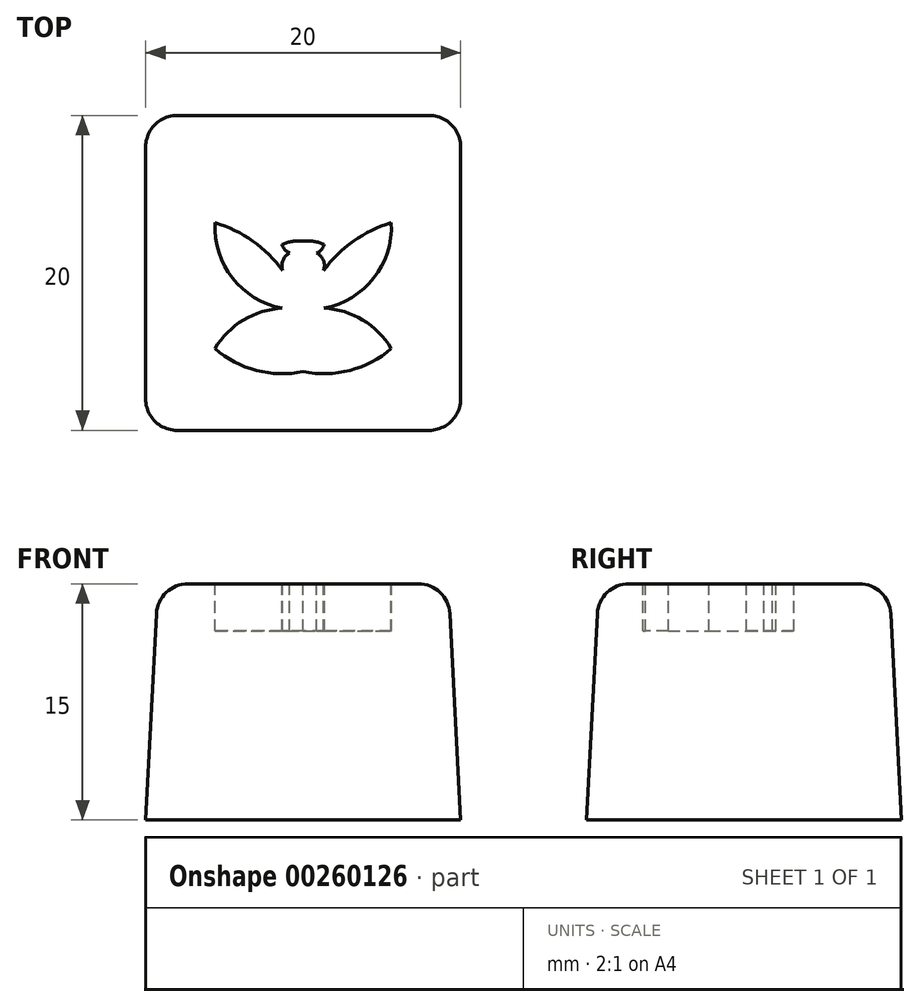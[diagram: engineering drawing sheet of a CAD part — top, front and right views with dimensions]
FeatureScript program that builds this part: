
annotation { "Feature Type Name" : "Feature", "Feature Type Description" : "" }
export const myFeature = defineFeature(function(context is Context, id is Id, definition is map)
    precondition{}
    {
        {
            var Q0;
            Q0=qCreatedBy(makeId("Top.planeOp"),FACE);
            var sketch = newSketch(context, id + "F0", { "sketchPlane" : qUnion([Q0])});
            skLineSegment(sketch, "E0.bottom", {"start": v(-8.66, 8.2) * mm, "end": v(11.34, 8.2) * mm});
            skLineSegment(sketch, "E0.top", {"start": v(-8.66, -11.8) * mm, "end": v(11.34, -11.8) * mm});
            skLineSegment(sketch, "E0.left", {"start": v(-8.66, 8.2) * mm, "end": v(-8.66, -11.8) * mm});
            skLineSegment(sketch, "E0.right", {"start": v(11.34, 8.2) * mm, "end": v(11.34, -11.8) * mm});
            skSolve(sketch);
        }
        {
            var Q0;
            Q0 = qSketchRegion(id + "F0", true);
            extrude(context, id + "F1", {"entities" : qUnion([Q0]), "depth" : 15 * mm, "hasDraft" : true, "draftAngle" : 3 * degree, "draftPullDirection" : true});
        }
        {
            var Q0;
            Q0=makeQuery(id+"F1.opExtrude","CAP_EDGE",EDGE,{"disambiguationData":[OSD([sQuery(id+"F0.wireOp",EDGE,"E0.bottom")])],"isStart":false});
            var Q1;
            Q1=makeQuery(id+"F1.opExtrude","SWEPT_EDGE",EDGE,{"disambiguationData":[OSD([sQuery(id+"F0.wireOp",EDGE,"E0.bottom"),sQuery(id+"F0.wireOp",EDGE,"E0.right")])]});
            var Q2;
            Q2=makeQuery(id+"F1.opExtrude","SWEPT_EDGE",EDGE,{"disambiguationData":[OSD([sQuery(id+"F0.wireOp",EDGE,"E0.top"),sQuery(id+"F0.wireOp",EDGE,"E0.right")])]});
            var Q3;
            Q3=makeQuery(id+"F1.opExtrude","CAP_EDGE",EDGE,{"disambiguationData":[OSD([sQuery(id+"F0.wireOp",EDGE,"E0.right")])],"isStart":false});
            var Q4;
            Q4=makeQuery(id+"F1.opExtrude","CAP_EDGE",EDGE,{"disambiguationData":[OSD([sQuery(id+"F0.wireOp",EDGE,"E0.left")])],"isStart":false});
            var Q5;
            Q5=makeQuery(id+"F1.opExtrude","CAP_EDGE",EDGE,{"disambiguationData":[OSD([sQuery(id+"F0.wireOp",EDGE,"E0.top")])],"isStart":false});
            var Q6;
            Q6=makeQuery(id+"F1.opExtrude","SWEPT_EDGE",EDGE,{"disambiguationData":[OSD([sQuery(id+"F0.wireOp",EDGE,"E0.bottom"),sQuery(id+"F0.wireOp",EDGE,"E0.left")])]});
            var Q7;
            Q7=makeQuery(id+"F1.opExtrude","SWEPT_EDGE",EDGE,{"disambiguationData":[OSD([sQuery(id+"F0.wireOp",EDGE,"E0.top"),sQuery(id+"F0.wireOp",EDGE,"E0.left")])]});
            fillet(context, id + "F2", {"entities" : qUnion([Q0, Q1, Q2, Q3, Q4, Q5, Q6, Q7]), "radius" : 2 * mm, "tangentPropagation" : true, "allowEdgeOverflow" : false});
        }
        {
            var Q0;
            Q0=makeQuery(id+"F1.opExtrude","CAP_FACE",FACE,{"disambiguationData":[OSD([sQuery(id+"F0.wireOp",EDGE,"E0.bottom"),sQuery(id+"F0.wireOp",EDGE,"E0.top"),sQuery(id+"F0.wireOp",EDGE,"E0.left"),sQuery(id+"F0.wireOp",EDGE,"E0.right")])],"isStart":false});
            var sketch = newSketch(context, id + "F3", { "sketchPlane" : qUnion([Q0])});
            skLineSegment(sketch, "E1", {"start": v(1.34, 5.5) * mm, "end": v(1.34, -9.12) * mm});
            skArc(sketch, "E2", {"start": v(-4.26, -6.62) * mm, "mid": v(-1.63, -8) * mm, "end": v(1.34, -8.08) * mm});
            skArc(sketch, "E3", {"start": v(0, -4.05) * mm, "mid": v(-2.45, -4.8) * mm, "end": v(-4.26, -6.62) * mm});
            skArc(sketch, "E4", {"start": v(-4.26, 1.38) * mm, "mid": v(-3.15, -2.14) * mm, "end": v(0, -4.05) * mm});
            skArc(sketch, "E5", {"start": v(0.03, -1.66) * mm, "mid": v(-1.86, 0.21) * mm, "end": v(-4.26, 1.38) * mm});
            skArc(sketch, "E6", {"start": v(0.47, -0.54) * mm, "mid": v(0.05, -1.02) * mm, "end": v(0.03, -1.66) * mm});
            skArc(sketch, "E7", {"start": v(0, 0) * mm, "mid": v(0.17, -0.33) * mm, "end": v(0.47, -0.54) * mm});
            skArc(sketch, "E8", {"start": v(1.34, 0.2) * mm, "mid": v(0.66, 0.19) * mm, "end": v(0, 0) * mm});
            skArc(sketch, "E9.MirrorCS", {"start": v(1.34, 0.2) * mm, "mid": v(2.02, 0.19) * mm, "end": v(2.68, 0) * mm});
            skArc(sketch, "E10.MirrorCS", {"start": v(2.68, 0) * mm, "mid": v(2.5, -0.33) * mm, "end": v(2.2, -0.54) * mm});
            skArc(sketch, "E11.MirrorCS", {"start": v(2.2, -0.54) * mm, "mid": v(2.63, -1.02) * mm, "end": v(2.64, -1.66) * mm});
            skArc(sketch, "E12.MirrorCS", {"start": v(2.64, -1.66) * mm, "mid": v(4.54, 0.21) * mm, "end": v(6.94, 1.38) * mm});
            skArc(sketch, "E13.MirrorCS", {"start": v(6.94, 1.38) * mm, "mid": v(5.83, -2.14) * mm, "end": v(2.68, -4.05) * mm});
            skArc(sketch, "E14.MirrorCS", {"start": v(2.68, -4.05) * mm, "mid": v(5.12, -4.8) * mm, "end": v(6.94, -6.62) * mm});
            skArc(sketch, "E15.MirrorCS", {"start": v(6.94, -6.62) * mm, "mid": v(4.3, -8) * mm, "end": v(1.34, -8.08) * mm});
            skSolve(sketch);
        }
        {
            var Q0;
            Q0 = qSketchRegion(id + "F3", true);
            extrude(context, id + "F4", {"entities" : qUnion([Q0]), "operationType" : NewBodyOperationType.REMOVE, "oppositeDirection" : true, "depth" : 3 * mm});
        }
    });
